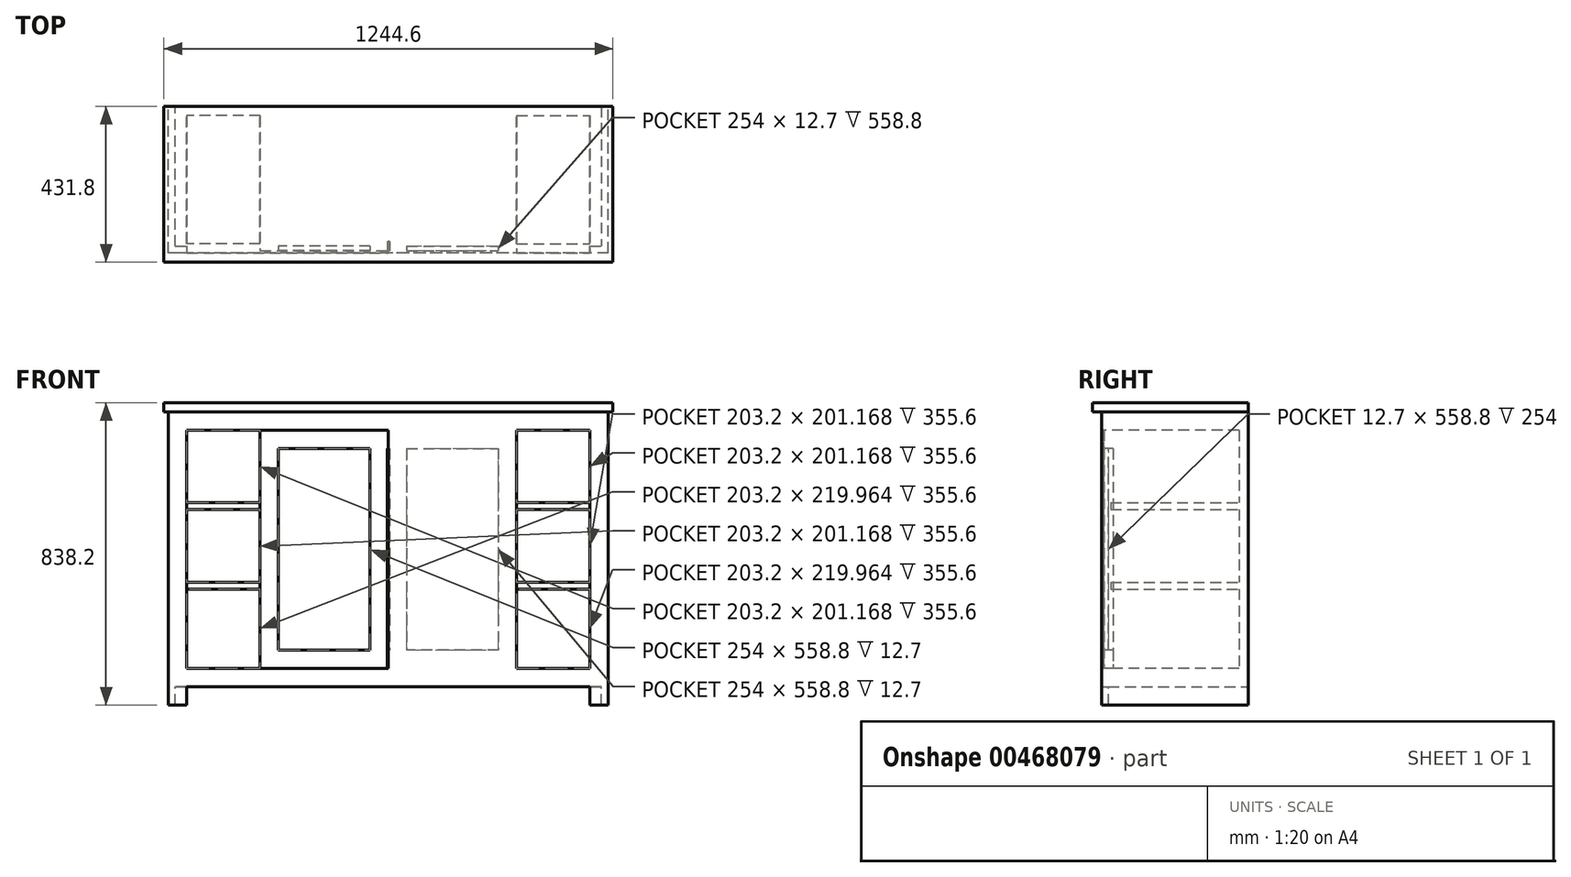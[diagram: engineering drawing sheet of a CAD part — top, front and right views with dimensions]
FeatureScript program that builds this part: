
annotation { "Feature Type Name" : "Feature", "Feature Type Description" : "" }
export const myFeature = defineFeature(function(context is Context, id is Id, definition is map)
    precondition{}
    {
        {
            var Q0;
            Q0=qCreatedBy(makeId("Front.planeOp"),FACE);
            var sketch = newSketch(context, id + "F0", { "sketchPlane" : qUnion([Q0])});
            skLineSegment(sketch, "E0.bottom", {"start": v(609.6, 381) * mm, "end": v(-609.6, 381) * mm});
            skLineSegment(sketch, "E0.top", {"start": v(609.6, -381) * mm, "end": v(-609.6, -381) * mm});
            skLineSegment(sketch, "E0.left", {"start": v(609.6, 381) * mm, "end": v(609.6, -381) * mm});
            skLineSegment(sketch, "E0.right", {"start": v(-609.6, 381) * mm, "end": v(-609.6, -381) * mm});
            skPoint(sketch, "E0.middle", {"position": v(0, 0) * mm});
            skSolve(sketch);
        }
        {
            var Q0;
            Q0 = qSketchRegion(id + "F0", true);
            extrude(context, id + "F1", {"entities" : qUnion([Q0]), "depth" : 406.4 * mm});
        }
        {
            var Q0;
            Q0=makeQuery(id+"F1.opExtrude","SWEPT_FACE",FACE,{"disambiguationData":[OSD([sQuery(id+"F0.wireOp",EDGE,"E0.top")])]});
            var sketch = newSketch(context, id + "F2", { "sketchPlane" : qUnion([Q0])});
            skLineSegment(sketch, "E1", {"start": v(-609.6, 406.4) * mm, "end": v(-571.5, 406.4) * mm});
            skLineSegment(sketch, "E2", {"start": v(-571.5, 406.4) * mm, "end": v(-571.5, 368.3) * mm});
            skLineSegment(sketch, "E3", {"start": v(-571.5, 368.3) * mm, "end": v(-609.6, 368.3) * mm});
            skLineSegment(sketch, "E4", {"start": v(-609.6, 0) * mm, "end": v(-609.6, 38.1) * mm});
            skLineSegment(sketch, "E5", {"start": v(-609.6, 38.1) * mm, "end": v(-571.5, 38.1) * mm});
            skLineSegment(sketch, "E6", {"start": v(-571.5, 38.1) * mm, "end": v(-571.5, 0) * mm});
            skLineSegment(sketch, "E7", {"start": v(609.6, 406.4) * mm, "end": v(571.5, 406.4) * mm});
            skLineSegment(sketch, "E8", {"start": v(571.5, 406.4) * mm, "end": v(571.5, 368.3) * mm});
            skLineSegment(sketch, "E9", {"start": v(571.5, 368.3) * mm, "end": v(609.6, 368.3) * mm});
            skLineSegment(sketch, "E10", {"start": v(609.6, 0) * mm, "end": v(609.6, 38.1) * mm});
            skLineSegment(sketch, "E11", {"start": v(609.6, 38.1) * mm, "end": v(571.5, 38.1) * mm});
            skLineSegment(sketch, "E12", {"start": v(571.5, 38.1) * mm, "end": v(571.5, 0) * mm});
            skSolve(sketch);
        }
        {
            var Q0;
            {var subQ0=sQuery(id+"F2.wireOp",EDGE,"E1");Q0=makeQuery(id+"F2.imprint","IMPRINT",FACE,{"disambiguationData":[TD([[makeQuery(id+"F2.imprint","IMPRINT",EDGE,{"derivedFrom":subQ0}),1.0]])]});}
            var Q1;
            {var subQ0=sQuery(id+"F2.wireOp",EDGE,"E4");Q1=makeQuery(id+"F2.imprint","IMPRINT",FACE,{"disambiguationData":[TD([[makeQuery(id+"F2.imprint","IMPRINT",EDGE,{"derivedFrom":subQ0}),1.0]])]});}
            var Q2;
            {var subQ0=sQuery(id+"F2.wireOp",EDGE,"E7");Q2=makeQuery(id+"F2.imprint","IMPRINT",FACE,{"disambiguationData":[TD([[makeQuery(id+"F2.imprint","IMPRINT",EDGE,{"derivedFrom":subQ0}),1.0]])]});}
            var Q3;
            {var subQ0=sQuery(id+"F2.wireOp",EDGE,"E10");Q3=makeQuery(id+"F2.imprint","IMPRINT",FACE,{"disambiguationData":[TD([[makeQuery(id+"F2.imprint","IMPRINT",EDGE,{"derivedFrom":subQ0}),-1.0]])]});}
            extrude(context, id + "F3", {"entities" : qUnion([Q0, Q1, Q2, Q3]), "operationType" : NewBodyOperationType.ADD, "depth" : 50.8 * mm});
        }
        {
            var Q0;
            Q0=makeQuery(id+"F1.opExtrude","SWEPT_FACE",FACE,{"disambiguationData":[OSD([sQuery(id+"F0.wireOp",EDGE,"E0.bottom")])]});
            var sketch = newSketch(context, id + "F4", { "sketchPlane" : qUnion([Q0])});
            skLineSegment(sketch, "E13", {"start": v(-609.6, 0) * mm, "end": v(-622.3, 0) * mm});
            skLineSegment(sketch, "E14", {"start": v(-622.3, 0) * mm, "end": v(-622.3, -406.4) * mm});
            skLineSegment(sketch, "E15", {"start": v(-622.3, -406.4) * mm, "end": v(-622.3, -431.8) * mm});
            skLineSegment(sketch, "E16", {"start": v(-622.3, -431.8) * mm, "end": v(622.3, -431.8) * mm});
            skLineSegment(sketch, "E17", {"start": v(622.3, -431.8) * mm, "end": v(622.3, 0) * mm});
            skLineSegment(sketch, "E18", {"start": v(622.3, 0) * mm, "end": v(609.6, 0) * mm});
            skLineSegment(sketch, "E19", {"start": v(609.6, 0) * mm, "end": v(-609.6, 0) * mm});
            skSolve(sketch);
        }
        {
            var Q0;
            Q0=makeQuery(id+"F4.imprint","IMPRINT",FACE,{"disambiguationData":[TD([[makeQuery(id+"F4.imprint","IMPRINT",EDGE,{"derivedFrom":sQuery(id+"F4.wireOp",EDGE,"E19")}),1.0]])]});
            var Q1;
            Q1=makeQuery(id+"F4.imprint","IMPRINT",FACE,{"disambiguationData":[TD([[makeQuery(id+"F4.imprint","IMPRINT",EDGE,{"derivedFrom":sQuery(id+"F4.wireOp",EDGE,"E13")}),1.0]])]});
            extrude(context, id + "F5", {"entities" : qUnion([Q0, Q1]), "operationType" : NewBodyOperationType.ADD, "depth" : 25.4 * mm});
        }
        {
            var Q0;
            Q0=makeQuery(id+"F3.boolean.opBoolean","MERGE",FACE,{"derivedFrom":[makeQuery(id+"F1.opExtrude","CAP_FACE",FACE,{"disambiguationData":[OSD([sQuery(id+"F0.wireOp",EDGE,"E0.bottom"),sQuery(id+"F0.wireOp",EDGE,"E0.top"),sQuery(id+"F0.wireOp",EDGE,"E0.left"),sQuery(id+"F0.wireOp",EDGE,"E0.right")])],"isStart":false}),makeQuery(id+"F3.opExtrude","SWEPT_FACE",FACE,{"disambiguationData":[OSD([sQuery(id+"F2.wireOp",EDGE,"E1")])]}),makeQuery(id+"F3.opExtrude","SWEPT_FACE",FACE,{"disambiguationData":[OSD([sQuery(id+"F2.wireOp",EDGE,"E7")])]})]});
            var sketch = newSketch(context, id + "F6", { "sketchPlane" : qUnion([Q0])});
            skLineSegment(sketch, "E20", {"start": v(-609.6, 381) * mm, "end": v(-558.8, 381) * mm});
            skLineSegment(sketch, "E21", {"start": v(-558.8, 381) * mm, "end": v(-558.8, -381) * mm});
            skLineSegment(sketch, "E22", {"start": v(-558.8, -381) * mm, "end": v(-558.8, -330.2) * mm});
            skLineSegment(sketch, "E23", {"start": v(-101.6, 381) * mm, "end": v(-101.6, 330.2) * mm});
            skLineSegment(sketch, "E24", {"start": v(-101.6, 330.2) * mm, "end": v(-558.8, 330.2) * mm});
            skLineSegment(sketch, "E25", {"start": v(-101.6, 330.2) * mm, "end": v(609.6, 330.2) * mm});
            skLineSegment(sketch, "E26", {"start": v(-558.8, -330.2) * mm, "end": v(609.6, -330.2) * mm});
            skLineSegment(sketch, "E27", {"start": v(609.6, -330.2) * mm, "end": v(558.8, -330.2) * mm});
            skLineSegment(sketch, "E28", {"start": v(558.8, -330.2) * mm, "end": v(558.8, 330.2) * mm});
            skLineSegment(sketch, "E29", {"start": v(0, 0) * mm, "end": v(0, 330.2) * mm});
            skLineSegment(sketch, "E30", {"start": v(0, 330.2) * mm, "end": v(0, -330.2) * mm});
            skLineSegment(sketch, "E31", {"start": v(0, 330.2) * mm, "end": v(355.6, 330.2) * mm});
            skLineSegment(sketch, "E32", {"start": v(355.6, 330.2) * mm, "end": v(355.6, -330.2) * mm});
            skLineSegment(sketch, "E33", {"start": v(355.6, -330.2) * mm, "end": v(-355.6, -330.2) * mm});
            skLineSegment(sketch, "E34", {"start": v(-355.6, -330.2) * mm, "end": v(-355.6, 330.2) * mm});
            skSolve(sketch);
        }
        {
            var Q0;
            {var subQ8=sQuery(id+"F6.wireOp",EDGE,"E34");Q0=makeQuery(id+"F6.imprint","IMPRINT",FACE,{"disambiguationData":[TD([[makeQuery(id+"F6.imprint","IMPRINT",EDGE,{"derivedFrom":subQ8}),-1.0]])]});}
            var Q1;
            {var subQ1=sQuery(id+"F6.wireOp",EDGE,"E31");Q1=makeQuery(id+"F6.imprint","IMPRINT",FACE,{"disambiguationData":[TD([[makeQuery(id+"F6.imprint","IMPRINT",EDGE,{"derivedFrom":subQ1}),-1.0]])]});}
            extrude(context, id + "F7", {"entities" : qUnion([Q0, Q1]), "operationType" : NewBodyOperationType.REMOVE, "oppositeDirection" : true, "depth" : 6.35 * mm});
        }
        {
            var Q0;
            {var subQ5=sQuery(id+"F6.wireOp",EDGE,"E34");Q0=makeQuery(id+"F6.imprint","IMPRINT",FACE,{"disambiguationData":[TD([[makeQuery(id+"F6.imprint","IMPRINT",EDGE,{"derivedFrom":subQ5}),1.0]])]});}
            var Q1;
            {var subQ0=sQuery(id+"F6.wireOp",EDGE,"E28");Q1=makeQuery(id+"F6.imprint","IMPRINT",FACE,{"disambiguationData":[TD([[makeQuery(id+"F6.imprint","IMPRINT",EDGE,{"derivedFrom":subQ0}),1.0]])]});}
            extrude(context, id + "F8", {"entities" : qUnion([Q0, Q1]), "operationType" : NewBodyOperationType.REMOVE, "oppositeDirection" : true, "depth" : 381 * mm});
        }
        {
            var Q0;
            Q0=makeQuery(id+"F7.boolean.opBoolean","COPY",FACE,{"derivedFrom":makeQuery(id+"F7.opExtrude","CAP_FACE",FACE,{"disambiguationData":[OSD([sQuery(id+"F6.wireOp",EDGE,"E24"),sQuery(id+"F6.wireOp",EDGE,"E25"),sQuery(id+"F6.wireOp",EDGE,"E31"),sQuery(id+"F6.wireOp",EDGE,"E32"),sQuery(id+"F6.wireOp",EDGE,"E33"),sQuery(id+"F6.wireOp",EDGE,"E34")])],"isStart":false})});
            var sketch = newSketch(context, id + "F9", { "sketchPlane" : qUnion([Q0])});
            skLineSegment(sketch, "E35.0", {"start": v(-304.8, -330.2) * mm, "end": v(-304.8, 330.2) * mm});
            skLineSegment(sketch, "E36.0", {"start": v(-558.8, 279.4) * mm, "end": v(558.8, 279.4) * mm});
            skLineSegment(sketch, "E37.0", {"start": v(304.8, 330.2) * mm, "end": v(304.8, -330.2) * mm});
            skLineSegment(sketch, "E38.0", {"start": v(558.8, -279.4) * mm, "end": v(-558.8, -279.4) * mm});
            skLineSegment(sketch, "E39", {"start": v(0, 279.4) * mm, "end": v(0, -279.4) * mm});
            skLineSegment(sketch, "E40.0", {"start": v(-50.8, 279.4) * mm, "end": v(-50.8, -279.4) * mm});
            skLineSegment(sketch, "E41.0", {"start": v(50.8, 279.4) * mm, "end": v(50.8, -279.4) * mm});
            skLineSegment(sketch, "E42.0", {"start": v(-3.18, 279.4) * mm, "end": v(-3.18, -279.4) * mm});
            skLineSegment(sketch, "E43.MirrorCS", {"start": v(3.17, 279.4) * mm, "end": v(3.17, -279.4) * mm});
            skLineSegment(sketch, "E44", {"start": v(3.17, 279.4) * mm, "end": v(3.17, 330.2) * mm});
            skLineSegment(sketch, "E45", {"start": v(-3.18, 279.4) * mm, "end": v(-3.18, 330.2) * mm});
            skLineSegment(sketch, "E46", {"start": v(-3.18, -279.4) * mm, "end": v(-3.18, -330.2) * mm});
            skPoint(sketch, "E46.endSnap0", {"position": v(0, -330.2) * mm});
            skLineSegment(sketch, "E47", {"start": v(3.17, -279.4) * mm, "end": v(3.17, -330.2) * mm});
            skSolve(sketch);
        }
        {
            var Q0;
            {var subQ5=sQuery(id+"F9.wireOp",EDGE,"E40.0");Q0=makeQuery(id+"F9.imprint","IMPRINT",FACE,{"disambiguationData":[TD([[makeQuery(id+"F9.imprint","IMPRINT",EDGE,{"derivedFrom":subQ5}),-1.0]])]});}
            var Q1;
            {var subQ0=sQuery(id+"F9.wireOp",EDGE,"E41.0");Q1=makeQuery(id+"F9.imprint","IMPRINT",FACE,{"disambiguationData":[TD([[makeQuery(id+"F9.imprint","IMPRINT",EDGE,{"derivedFrom":subQ0}),1.0]])]});}
            extrude(context, id + "F10", {"entities" : qUnion([Q0, Q1]), "operationType" : NewBodyOperationType.REMOVE, "oppositeDirection" : true, "depth" : 12.7 * mm});
        }
        {
            var Q0;
            {var subQ0=sQuery(id+"F9.wireOp",EDGE,"E39");Q0=makeQuery(id+"F9.imprint","IMPRINT",FACE,{"disambiguationData":[TD([[makeQuery(id+"F9.imprint","IMPRINT",EDGE,{"derivedFrom":subQ0}),1.0]])]});}
            var Q1;
            {var subQ0=sQuery(id+"F9.wireOp",EDGE,"E39");Q1=makeQuery(id+"F9.imprint","IMPRINT",FACE,{"disambiguationData":[TD([[makeQuery(id+"F9.imprint","IMPRINT",EDGE,{"derivedFrom":subQ0}),-1.0]])]});}
            var Q2;
            {var subQ1=sQuery(id+"F9.wireOp",EDGE,"E46");Q2=makeQuery(id+"F9.imprint","IMPRINT",FACE,{"disambiguationData":[TD([[makeQuery(id+"F9.imprint","IMPRINT",EDGE,{"derivedFrom":subQ1}),1.0]])]});}
            var Q3;
            {var subQ3=sQuery(id+"F9.wireOp",EDGE,"E44");Q3=makeQuery(id+"F9.imprint","IMPRINT",FACE,{"disambiguationData":[TD([[makeQuery(id+"F9.imprint","IMPRINT",EDGE,{"derivedFrom":subQ3}),1.0]])]});}
            extrude(context, id + "F11", {"entities" : qUnion([Q0, Q1, Q2, Q3]), "operationType" : NewBodyOperationType.REMOVE, "oppositeDirection" : true, "depth" : 25.4 * mm});
        }
        {
            var Q0;
            Q0=makeQuery(id+"F8.boolean.opBoolean","COPY",FACE,{"derivedFrom":makeQuery(id+"F8.opExtrude","CAP_FACE",FACE,{"disambiguationData":[OSD([sQuery(id+"F6.wireOp",EDGE,"E21"),sQuery(id+"F6.wireOp",EDGE,"E24"),sQuery(id+"F6.wireOp",EDGE,"E26"),sQuery(id+"F6.wireOp",EDGE,"E34")])],"isStart":false})});
            var sketch = newSketch(context, id + "F12", { "sketchPlane" : qUnion([Q0])});
            skLineSegment(sketch, "E48", {"start": v(0, 0) * mm, "end": v(0, 412.65) * mm});
            skLineSegment(sketch, "E49", {"start": v(-355.6, 330.2) * mm, "end": v(-355.6, 129.03) * mm});
            skLineSegment(sketch, "E50", {"start": v(-355.6, 129.03) * mm, "end": v(-355.6, 109.98) * mm});
            skLineSegment(sketch, "E51", {"start": v(-355.6, 109.98) * mm, "end": v(-355.6, -91.19) * mm});
            skLineSegment(sketch, "E52", {"start": v(-355.6, -91.19) * mm, "end": v(-355.6, -110.24) * mm});
            skLineSegment(sketch, "E53", {"start": v(-355.6, -110.24) * mm, "end": v(-558.8, -110.24) * mm});
            skLineSegment(sketch, "E54", {"start": v(-355.6, -91.19) * mm, "end": v(-558.8, -91.19) * mm});
            skLineSegment(sketch, "E55", {"start": v(-355.6, 129.03) * mm, "end": v(-558.8, 129.03) * mm});
            skLineSegment(sketch, "E56", {"start": v(-355.6, 109.98) * mm, "end": v(-558.8, 109.98) * mm});
            skLineSegment(sketch, "E57.MirrorCS", {"start": v(355.6, 129.03) * mm, "end": v(558.8, 129.03) * mm});
            skLineSegment(sketch, "E58.MirrorCS", {"start": v(355.6, 109.98) * mm, "end": v(558.8, 109.98) * mm});
            skLineSegment(sketch, "E59.MirrorCS", {"start": v(355.6, -91.19) * mm, "end": v(558.8, -91.19) * mm});
            skLineSegment(sketch, "E60.MirrorCS", {"start": v(355.6, -110.24) * mm, "end": v(558.8, -110.24) * mm});
            skLineSegment(sketch, "E61", {"start": v(355.6, 129.03) * mm, "end": v(355.6, 109.98) * mm});
            skLineSegment(sketch, "E62", {"start": v(355.6, -91.19) * mm, "end": v(355.6, -110.24) * mm});
            skLineSegment(sketch, "E63", {"start": v(558.8, -91.19) * mm, "end": v(558.8, -110.24) * mm});
            skLineSegment(sketch, "E64", {"start": v(558.8, 129.03) * mm, "end": v(558.8, 109.98) * mm});
            skSolve(sketch);
        }
        {
            var Q0;
            Q0=makeQuery(id+"F12.imprint","IMPRINT",FACE,{"disambiguationData":[TD([[makeQuery(id+"F12.imprint","IMPRINT",EDGE,{"derivedFrom":sQuery(id+"F12.wireOp",EDGE,"E50")}),1.0]])]});
            var Q1;
            Q1=makeQuery(id+"F12.imprint","IMPRINT",FACE,{"disambiguationData":[TD([[makeQuery(id+"F12.imprint","IMPRINT",EDGE,{"derivedFrom":sQuery(id+"F12.wireOp",EDGE,"E52")}),1.0]])]});
            var Q2;
            Q2=makeQuery(id+"F12.imprint","IMPRINT",FACE,{"disambiguationData":[TD([[makeQuery(id+"F12.imprint","IMPRINT",EDGE,{"derivedFrom":sQuery(id+"F12.wireOp",EDGE,"E59.MirrorCS")}),-1.0]])]});
            var Q3;
            Q3=makeQuery(id+"F12.imprint","IMPRINT",FACE,{"disambiguationData":[TD([[makeQuery(id+"F12.imprint","IMPRINT",EDGE,{"derivedFrom":sQuery(id+"F12.wireOp",EDGE,"E57.MirrorCS")}),-1.0]])]});
            extrude(context, id + "F13", {"entities" : qUnion([Q0, Q1, Q2, Q3]), "operationType" : NewBodyOperationType.ADD, "depth" : 355.6 * mm});
        }
        {
            var Q0;
            Q0=makeQuery(id+"F3.opExtrude","CAP_FACE",FACE,{"disambiguationData":[OSD([sQuery(id+"F0.wireOp",EDGE,"E0.top"),sQuery(id+"F0.wireOp",EDGE,"E0.right"),sQuery(id+"F2.wireOp",EDGE,"E1"),sQuery(id+"F2.wireOp",EDGE,"E2"),sQuery(id+"F2.wireOp",EDGE,"E3")])],"isStart":false});
            var Q1;
            Q1=makeQuery(id+"F3.opExtrude","CAP_FACE",FACE,{"disambiguationData":[OSD([sQuery(id+"F0.wireOp",EDGE,"E0.top"),sQuery(id+"F0.wireOp",EDGE,"E0.left"),sQuery(id+"F2.wireOp",EDGE,"E7"),sQuery(id+"F2.wireOp",EDGE,"E8"),sQuery(id+"F2.wireOp",EDGE,"E9")])],"isStart":false});
            var Q2;
            Q2=makeQuery(id+"F3.opExtrude","CAP_FACE",FACE,{"disambiguationData":[OSD([sQuery(id+"F0.wireOp",EDGE,"E0.top"),sQuery(id+"F2.wireOp",EDGE,"E10"),sQuery(id+"F2.wireOp",EDGE,"E11"),sQuery(id+"F2.wireOp",EDGE,"E12")])],"isStart":false});
            var Q3;
            Q3=makeQuery(id+"F3.opExtrude","CAP_FACE",FACE,{"disambiguationData":[OSD([sQuery(id+"F0.wireOp",EDGE,"E0.top"),sQuery(id+"F2.wireOp",EDGE,"E4"),sQuery(id+"F2.wireOp",EDGE,"E5"),sQuery(id+"F2.wireOp",EDGE,"E6")])],"isStart":false});
            extrude(context, id + "F14", {"entities" : qUnion([Q0, Q1, Q2, Q3]), "operationType" : NewBodyOperationType.REMOVE, "oppositeDirection" : true, "depth" : 50.8 * mm, "offsetDistance" : 25.4 * mm});
        }
        {
            var Q0;
            {var subQ0=sQuery(id+"F0.wireOp",EDGE,"E0.top");Q0=makeQuery(id+"F14.boolean.opBoolean","MERGE",FACE,{"derivedFrom":[makeQuery(id+"F1.opExtrude","SWEPT_FACE",FACE,{"disambiguationData":[OSD([subQ0])]})],"fromTools":[makeQuery(id+"F14.opExtrude","CAP_FACE",FACE,{"disambiguationData":[OSD([subQ0,sQuery(id+"F0.wireOp",EDGE,"E0.right"),sQuery(id+"F2.wireOp",EDGE,"E1"),sQuery(id+"F2.wireOp",EDGE,"E2"),sQuery(id+"F2.wireOp",EDGE,"E3")])],"isStart":false}),makeQuery(id+"F14.opExtrude","CAP_FACE",FACE,{"disambiguationData":[OSD([subQ0,sQuery(id+"F2.wireOp",EDGE,"E4"),sQuery(id+"F2.wireOp",EDGE,"E5"),sQuery(id+"F2.wireOp",EDGE,"E6")])],"isStart":false}),makeQuery(id+"F14.opExtrude","CAP_FACE",FACE,{"disambiguationData":[OSD([subQ0,sQuery(id+"F0.wireOp",EDGE,"E0.left"),sQuery(id+"F2.wireOp",EDGE,"E7"),sQuery(id+"F2.wireOp",EDGE,"E8"),sQuery(id+"F2.wireOp",EDGE,"E9")])],"isStart":false}),makeQuery(id+"F14.opExtrude","CAP_FACE",FACE,{"disambiguationData":[OSD([subQ0,sQuery(id+"F2.wireOp",EDGE,"E10"),sQuery(id+"F2.wireOp",EDGE,"E11"),sQuery(id+"F2.wireOp",EDGE,"E12")])],"isStart":false})]});}
            var sketch = newSketch(context, id + "F15", { "sketchPlane" : qUnion([Q0])});
            skLineSegment(sketch, "E65", {"start": v(-609.6, 406.4) * mm, "end": v(-590.55, 406.4) * mm});
            skLineSegment(sketch, "E66", {"start": v(-590.55, 406.4) * mm, "end": v(-590.55, 0) * mm});
            skLineSegment(sketch, "E67", {"start": v(-590.55, 0) * mm, "end": v(-609.6, 0) * mm});
            skLineSegment(sketch, "E68", {"start": v(-609.6, 0) * mm, "end": v(-609.6, 406.4) * mm});
            skLineSegment(sketch, "E69", {"start": v(609.6, 0) * mm, "end": v(590.55, 0) * mm});
            skLineSegment(sketch, "E70", {"start": v(590.55, 0) * mm, "end": v(590.55, 406.4) * mm});
            skLineSegment(sketch, "E71", {"start": v(590.55, 406.4) * mm, "end": v(609.6, 406.4) * mm});
            skLineSegment(sketch, "E72", {"start": v(609.6, 406.4) * mm, "end": v(609.6, 0) * mm});
            skLineSegment(sketch, "E73", {"start": v(-609.6, 406.4) * mm, "end": v(-609.6, 387.35) * mm});
            skLineSegment(sketch, "E74", {"start": v(-609.6, 387.35) * mm, "end": v(-558.8, 387.35) * mm});
            skLineSegment(sketch, "E75", {"start": v(-558.8, 387.35) * mm, "end": v(-558.8, 406.4) * mm});
            skLineSegment(sketch, "E76", {"start": v(609.6, 406.4) * mm, "end": v(558.8, 406.4) * mm});
            skLineSegment(sketch, "E77", {"start": v(558.8, 406.4) * mm, "end": v(558.8, 387.35) * mm});
            skLineSegment(sketch, "E78", {"start": v(558.8, 387.35) * mm, "end": v(609.6, 387.35) * mm});
            skSolve(sketch);
        }
        {
            var Q0;
            Q0 = qSketchRegion(id + "F15", true);
            var Q1;
            {var subQ5=sQuery(id+"F15.wireOp",EDGE,"E75");Q1=makeQuery(id+"F15.imprint","IMPRINT",FACE,{"disambiguationData":[TD([[makeQuery(id+"F15.imprint","IMPRINT",EDGE,{"derivedFrom":subQ5}),1.0]])]});}
            extrude(context, id + "F16", {"entities" : qUnion([Q0, Q1]), "operationType" : NewBodyOperationType.ADD, "depth" : 50.8 * mm, "offsetDistance" : 25.4 * mm});
        }
    });
